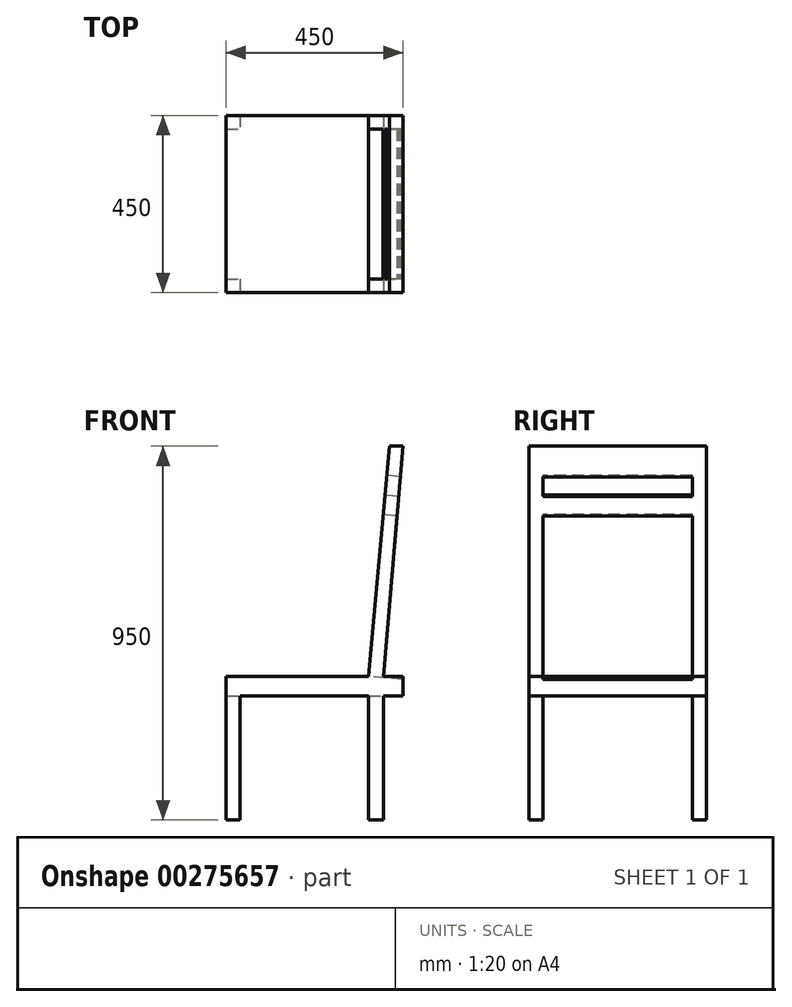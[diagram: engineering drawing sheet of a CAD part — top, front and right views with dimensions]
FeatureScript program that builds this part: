
annotation { "Feature Type Name" : "Feature", "Feature Type Description" : "" }
export const myFeature = defineFeature(function(context is Context, id is Id, definition is map)
    precondition{}
    {
        {
            var Q0;
            Q0=qCreatedBy(makeId("Top.planeOp"),FACE);
            var sketch = newSketch(context, id + "F0", { "sketchPlane" : qUnion([Q0])});
            skLineSegment(sketch, "E0.bottom", {"start": v(225, 225) * mm, "end": v(-225, 225) * mm});
            skLineSegment(sketch, "E0.top", {"start": v(225, -225) * mm, "end": v(-225, -225) * mm});
            skLineSegment(sketch, "E0.left", {"start": v(225, 225) * mm, "end": v(225, -225) * mm});
            skLineSegment(sketch, "E0.right", {"start": v(-225, 225) * mm, "end": v(-225, -225) * mm});
            skPoint(sketch, "E0.middle", {"position": v(0, 0) * mm});
            skSolve(sketch);
        }
        {
            var Q0;
            Q0=qSketchRegion(id+"F0",true);
            extrude(context, id + "F1", {"entities" : qUnion([Q0]), "depth" : 950 * mm});
        }
        {
            var Q0;
            Q0=makeQuery(id+"F1.opExtrude","SWEPT_FACE",FACE,{"disambiguationData":[OSD([sQuery(id+"F0.wireOp",EDGE,"E0.top")])]});
            var sketch = newSketch(context, id + "F2", { "sketchPlane" : qUnion([Q0])});
            skLineSegment(sketch, "E1.left", {"start": v(-225, 365.07) * mm, "end": v(-225, 360.07) * mm});
            skLineSegment(sketch, "E1.right", {"start": v(225, 365.06) * mm, "end": v(225, 360.06) * mm});
            skLineSegment(sketch, "E2.bottom", {"start": v(-225, 365.07) * mm, "end": v(225, 365.07) * mm});
            skLineSegment(sketch, "E2.top", {"start": v(-225, 315.07) * mm, "end": v(225, 315.07) * mm});
            skLineSegment(sketch, "E2.left", {"start": v(-225, 365.07) * mm, "end": v(-225, 315.07) * mm});
            skLineSegment(sketch, "E2.right", {"start": v(225, 365.07) * mm, "end": v(225, 315.07) * mm});
            skLineSegment(sketch, "E3", {"start": v(225, 360.06) * mm, "end": v(225, 315.07) * mm});
            skLineSegment(sketch, "E4", {"start": v(-225, 315.07) * mm, "end": v(-225, 365.07) * mm});
            skLineSegment(sketch, "E5", {"start": v(225, 950) * mm, "end": v(175, 365.07) * mm});
            skLineSegment(sketch, "E6", {"start": v(225, 950) * mm, "end": v(200, 657.53) * mm});
            skLineSegment(sketch, "E7", {"start": v(190, 950) * mm, "end": v(136.75, 365.07) * mm});
            skLineSegment(sketch, "E8", {"start": v(175, 365.07) * mm, "end": v(175, 0) * mm});
            skLineSegment(sketch, "E9", {"start": v(136.75, 365.07) * mm, "end": v(136.75, 0) * mm});
            skLineSegment(sketch, "E10.bottom", {"start": v(-225, 0) * mm, "end": v(-190, 0) * mm});
            skLineSegment(sketch, "E10.top", {"start": v(-225, 0) * mm, "end": v(-190, 0) * mm});
            skLineSegment(sketch, "E10.left", {"start": v(-225, 0) * mm, "end": v(-225, 0) * mm});
            skLineSegment(sketch, "E10.right", {"start": v(-190, 0) * mm, "end": v(-190, 0) * mm});
            skLineSegment(sketch, "E11.bottom", {"start": v(-190, 0) * mm, "end": v(-225, 0) * mm});
            skLineSegment(sketch, "E11.top", {"start": v(-190, 315.07) * mm, "end": v(-225, 315.07) * mm});
            skLineSegment(sketch, "E11.left", {"start": v(-190, 0) * mm, "end": v(-190, 315.07) * mm});
            skLineSegment(sketch, "E11.right", {"start": v(-225, 0) * mm, "end": v(-225, 315.07) * mm});
            skSolve(sketch);
        }
        {
            var Q0;
            {var subQ4=sQuery(id+"F2.wireOp",EDGE,"E7");Q0=makeQuery(id+"F2.imprint","IMPRINT",FACE,{"disambiguationData":[TD([[makeQuery(id+"F2.imprint","IMPRINT",EDGE,{"derivedFrom":subQ4}),-1.0]])]});}
            var Q1;
            {var subQ4=sQuery(id+"F2.wireOp",EDGE,"E5");Q1=makeQuery(id+"F2.imprint","IMPRINT",FACE,{"disambiguationData":[TD([[makeQuery(id+"F2.imprint","IMPRINT",EDGE,{"derivedFrom":subQ4}),1.0]])]});}
            var Q2;
            {var subQ0=sQuery(id+"F2.wireOp",EDGE,"E3");Q2=makeQuery(id+"F2.imprint","IMPRINT",FACE,{"disambiguationData":[TD([[makeQuery(id+"F2.imprint","IMPRINT",EDGE,{"derivedFrom":subQ0}),-1.0]])]});}
            var Q3;
            {var subQ1=sQuery(id+"F0.wireOp",EDGE,"E0.top");var subQ4=sQuery(id+"F2.wireOp",EDGE,"E8");var subQ6=makeQuery(id+"F1.opExtrude","CAP_EDGE",EDGE,{"disambiguationData":[OSD([subQ1])],"isStart":true});var subQ7=makeQuery(id+"F2.imprint","INTERSECT",VERTEX,{"derivedFrom":[subQ6,subQ4]});Q3=makeQuery(id+"F2.imprint","IMPRINT",FACE,{"disambiguationData":[TD([[makeQuery(id+"F2.imprint","IMPRINT",EDGE,{"disambiguationData":[TD([[subQ7,1.0]])],"derivedFrom":subQ4}),1.0]])]});}
            var Q4;
            {var subQ0=sQuery(id+"F2.wireOp",EDGE,"E11.left");Q4=makeQuery(id+"F2.imprint","IMPRINT",FACE,{"disambiguationData":[TD([[makeQuery(id+"F2.imprint","IMPRINT",EDGE,{"derivedFrom":subQ0}),-1.0]])]});}
            extrude(context, id + "F3", {"entities" : qUnion([Q0, Q1, Q2, Q3, Q4]), "operationType" : NewBodyOperationType.REMOVE, "endBound" : BoundingType.THROUGH_ALL, "oppositeDirection" : true, "depth" : 25 * mm});
        }
        {
            var Q0;
            Q0=makeQuery(id+"F3.boolean.opBoolean","COPY",FACE,{"derivedFrom":makeQuery(id+"F3.opExtrude","SWEPT_FACE",FACE,{"disambiguationData":[OSD([sQuery(id+"F2.wireOp",EDGE,"E8")])]})});
            var sketch = newSketch(context, id + "F4", { "sketchPlane" : qUnion([Q0])});
            skLineSegment(sketch, "E12", {"start": v(-190, 0) * mm, "end": v(-190, 172.17) * mm});
            skLineSegment(sketch, "E13", {"start": v(-190, 172.17) * mm, "end": v(-190, 330.38) * mm});
            skLineSegment(sketch, "E14", {"start": v(-190, 330.38) * mm, "end": v(190, 330.38) * mm});
            skLineSegment(sketch, "E15", {"start": v(190, 330.38) * mm, "end": v(190, 0) * mm});
            skSolve(sketch);
        }
        {
            var Q0;
            Q0 = qSketchRegion(id + "F4", true);
            var Q1;
            {var subQ1=sQuery(id+"F4.wireOp",EDGE,"E12");Q1=makeQuery(id+"F4.imprint","IMPRINT",FACE,{"disambiguationData":[TD([[makeQuery(id+"F4.imprint","IMPRINT",EDGE,{"derivedFrom":subQ1}),-1.0]])]});}
            extrude(context, id + "F5", {"entities" : qUnion([Q0, Q1]), "operationType" : NewBodyOperationType.REMOVE, "endBound" : BoundingType.THROUGH_ALL, "oppositeDirection" : true, "depth" : 25 * mm});
        }
        {
            var Q0;
            Q0=makeQuery(id+"F3.boolean.opBoolean","COPY",FACE,{"derivedFrom":makeQuery(id+"F3.opExtrude","SWEPT_FACE",FACE,{"disambiguationData":[OSD([sQuery(id+"F2.wireOp",EDGE,"E7")])]})});
            var sketch = newSketch(context, id + "F6", { "sketchPlane" : qUnion([Q0])});
            skLineSegment(sketch, "E16", {"start": v(-190, 375.96) * mm, "end": v(-190, 888.31) * mm});
            skLineSegment(sketch, "E17", {"start": v(-190, 888.31) * mm, "end": v(190, 888.31) * mm});
            skLineSegment(sketch, "E18", {"start": v(190, 888.31) * mm, "end": v(190, 375.96) * mm});
            skLineSegment(sketch, "E19", {"start": v(-190, 838.31) * mm, "end": v(190, 838.31) * mm});
            skLineSegment(sketch, "E20", {"start": v(-190, 788.31) * mm, "end": v(190, 788.31) * mm});
            skSolve(sketch);
        }
        {
            var Q0;
            {var subQ3=sQuery(id+"F6.wireOp",EDGE,"E20");Q0=makeQuery(id+"F6.imprint","IMPRINT",FACE,{"disambiguationData":[TD([[makeQuery(id+"F6.imprint","IMPRINT",EDGE,{"derivedFrom":subQ3}),-1.0]])]});}
            var Q1;
            {var subQ0=sQuery(id+"F6.wireOp",EDGE,"E17");Q1=makeQuery(id+"F6.imprint","IMPRINT",FACE,{"disambiguationData":[TD([[makeQuery(id+"F6.imprint","IMPRINT",EDGE,{"derivedFrom":subQ0}),-1.0]])]});}
            extrude(context, id + "F7", {"entities" : qUnion([Q0, Q1]), "operationType" : NewBodyOperationType.REMOVE, "endBound" : BoundingType.THROUGH_ALL, "oppositeDirection" : true, "depth" : 25 * mm});
        }
    });
